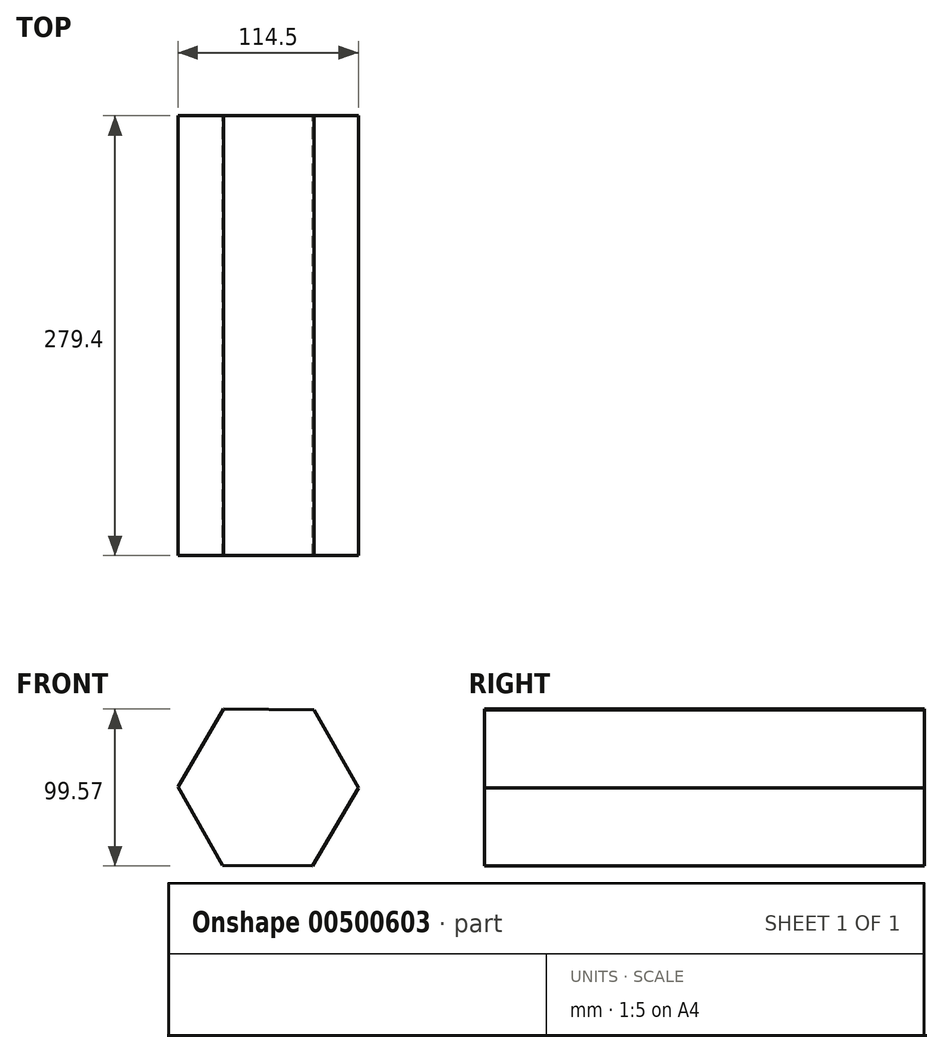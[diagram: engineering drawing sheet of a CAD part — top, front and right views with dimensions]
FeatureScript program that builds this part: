
annotation { "Feature Type Name" : "Feature", "Feature Type Description" : "" }
export const myFeature = defineFeature(function(context is Context, id is Id, definition is map)
    precondition{}
    {
        {
            var Q0;
            Q0=qCreatedBy(makeId("Front.planeOp"),FACE);
            var sketch = newSketch(context, id + "F0", { "sketchPlane" : qUnion([Q0])});
            skCircle(sketch, "E0.cCircle", {"center": v(0, 12.04) * mm, "radius": 57.25 * mm, "construction": true});
            skLineSegment(sketch, "E0.0", {"start": v(-28.27, 61.82) * mm, "end": v(28.98, 61.41) * mm});
            skLineSegment(sketch, "E0.1", {"start": v(28.98, 61.41) * mm, "end": v(57.25, 11.63) * mm});
            skLineSegment(sketch, "E0.2", {"start": v(57.25, 11.63) * mm, "end": v(28.27, -37.75) * mm});
            skLineSegment(sketch, "E0.3", {"start": v(28.27, -37.75) * mm, "end": v(-28.98, -37.34) * mm});
            skLineSegment(sketch, "E0.4", {"start": v(-28.98, -37.34) * mm, "end": v(-57.25, 12.44) * mm});
            skLineSegment(sketch, "E0.5", {"start": v(-57.25, 12.44) * mm, "end": v(-28.27, 61.82) * mm});
            skSolve(sketch);
        }
        {
            var Q0;
            Q0 = qSketchRegion(id + "F0", true);
            extrude(context, id + "F1", {"entities" : qUnion([Q0]), "depth" : 279.4 * mm});
        }
    });
